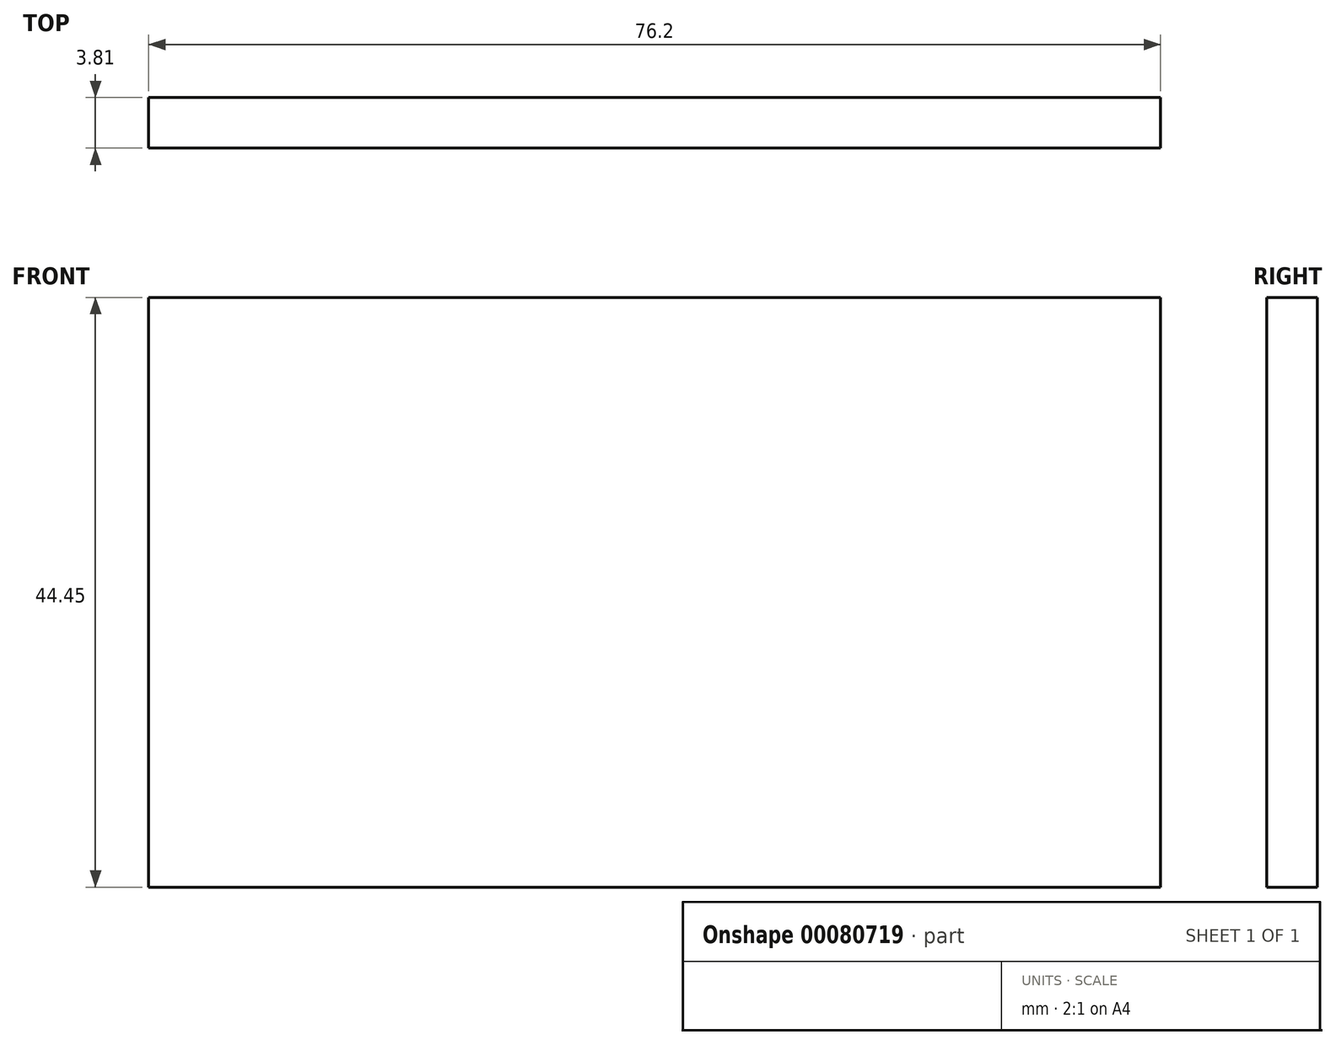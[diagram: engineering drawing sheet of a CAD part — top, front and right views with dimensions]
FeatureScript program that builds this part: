
annotation { "Feature Type Name" : "Feature", "Feature Type Description" : "" }
export const myFeature = defineFeature(function(context is Context, id is Id, definition is map)
    precondition{}
    {
        {
            var Q0;
            Q0=qCreatedBy(makeId("Front.planeOp"),FACE);
            var sketch = newSketch(context, id + "F0", { "sketchPlane" : qUnion([Q0])});
            skLineSegment(sketch, "E0.bottom", {"start": v(-38.5, 33.65) * mm, "end": v(37.7, 33.65) * mm});
            skLineSegment(sketch, "E0.top", {"start": v(-38.5, -10.8) * mm, "end": v(37.7, -10.8) * mm});
            skLineSegment(sketch, "E0.left", {"start": v(-38.5, 33.65) * mm, "end": v(-38.5, -10.8) * mm});
            skLineSegment(sketch, "E0.right", {"start": v(37.7, 33.65) * mm, "end": v(37.7, -10.8) * mm});
            skSolve(sketch);
        }
        {
            var Q0;
            Q0=makeQuery(id+"F0.imprint","IMPRINT",FACE,{"disambiguationData":[TD([[makeQuery(id+"F0.imprint","IMPRINT",EDGE,{"derivedFrom":sQuery(id+"F0.wireOp",EDGE,"E0.bottom")}),-1.0]])]});
            extrude(context, id + "F1", {"entities" : qUnion([Q0]), "depth" : 3.8 * mm});
        }
    });
